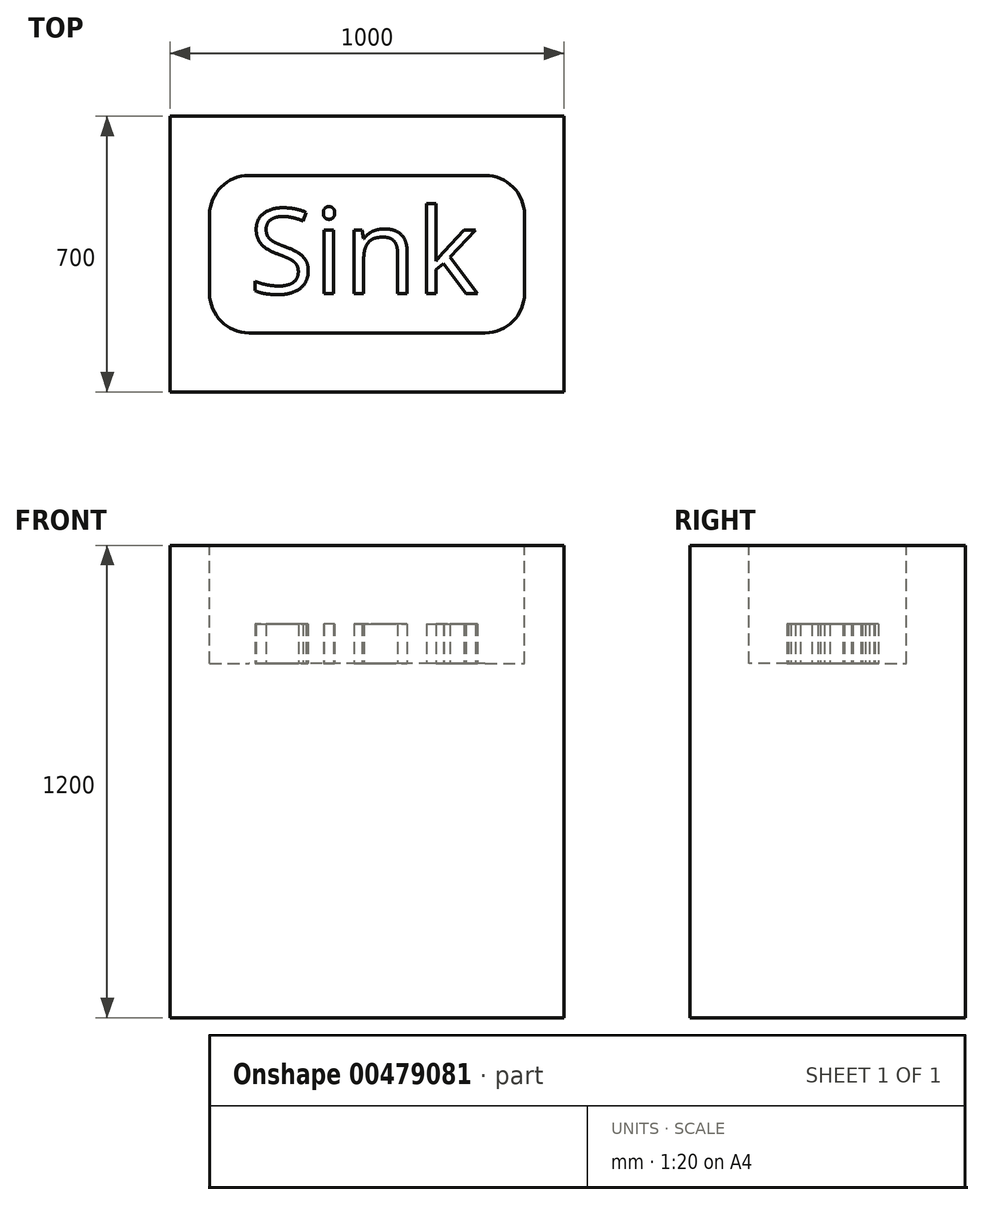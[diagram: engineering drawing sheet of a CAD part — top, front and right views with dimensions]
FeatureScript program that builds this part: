
annotation { "Feature Type Name" : "Feature", "Feature Type Description" : "" }
export const myFeature = defineFeature(function(context is Context, id is Id, definition is map)
    precondition{}
    {
        {
            var Q0;
            Q0=qCreatedBy(makeId("Top.planeOp"),FACE);
            var sketch = newSketch(context, id + "F0", { "sketchPlane" : qUnion([Q0])});
            skLineSegment(sketch, "E0.bottom", {"start": v(500, -350) * mm, "end": v(-500, -350) * mm});
            skLineSegment(sketch, "E0.top", {"start": v(500, 350) * mm, "end": v(-500, 350) * mm});
            skLineSegment(sketch, "E0.left", {"start": v(500, -350) * mm, "end": v(500, 350) * mm});
            skLineSegment(sketch, "E0.right", {"start": v(-500, -350) * mm, "end": v(-500, 350) * mm});
            skPoint(sketch, "E0.middle", {"position": v(0, 0) * mm});
            skSolve(sketch);
        }
        {
            var Q0;
            Q0 = qSketchRegion(id + "F0", true);
            extrude(context, id + "F1", {"entities" : qUnion([Q0]), "depth" : 1200 * mm});
        }
        {
            var Q0;
            Q0=makeQuery(id+"F1.opExtrude","CAP_FACE",FACE,{"disambiguationData":[OSD([sQuery(id+"F0.wireOp",EDGE,"E0.bottom"),sQuery(id+"F0.wireOp",EDGE,"E0.top"),sQuery(id+"F0.wireOp",EDGE,"E0.left"),sQuery(id+"F0.wireOp",EDGE,"E0.right")])],"isStart":false});
            var sketch = newSketch(context, id + "F2", { "sketchPlane" : qUnion([Q0])});
            skLineSegment(sketch, "E1.bottom", {"start": v(300, -200) * mm, "end": v(-300, -200) * mm});
            skLineSegment(sketch, "E1.top", {"start": v(300, 200) * mm, "end": v(-300, 200) * mm});
            skLineSegment(sketch, "E1.left", {"start": v(400, -100) * mm, "end": v(400, 100) * mm});
            skLineSegment(sketch, "E1.right", {"start": v(-400, -100) * mm, "end": v(-400, 100) * mm});
            skPoint(sketch, "E1.middle", {"position": v(0, 0) * mm});
            skPoint(sketch, "E2.visualSharp", {"position": v(-400, 200) * mm});
            skArc(sketch, "E2.filletArc", {"start": v(-300, 200) * mm, "mid": v(-370.71, 170.71) * mm, "end": v(-400, 100) * mm});
            skPoint(sketch, "E3.visualSharp", {"position": v(-400, -200) * mm});
            skArc(sketch, "E3.filletArc", {"start": v(-400, -100) * mm, "mid": v(-370.71, -170.71) * mm, "end": v(-300, -200) * mm});
            skPoint(sketch, "E4.visualSharp", {"position": v(400, -200) * mm});
            skArc(sketch, "E4.filletArc", {"start": v(300, -200) * mm, "mid": v(370.71, -170.71) * mm, "end": v(400, -100) * mm});
            skPoint(sketch, "E5.visualSharp", {"position": v(400, 200) * mm});
            skArc(sketch, "E5.filletArc", {"start": v(400, 100) * mm, "mid": v(370.71, 170.71) * mm, "end": v(300, 200) * mm});
            skSolve(sketch);
        }
        {
            var Q0;
            Q0 = qSketchRegion(id + "F2", true);
            extrude(context, id + "F3", {"entities" : qUnion([Q0]), "operationType" : NewBodyOperationType.REMOVE, "oppositeDirection" : true, "depth" : 300 * mm});
        }
        {
            var Q0;
            Q0=makeQuery(id+"F3.boolean.opBoolean","COPY",FACE,{"derivedFrom":makeQuery(id+"F3.opExtrude","CAP_FACE",FACE,{"disambiguationData":[OSD([sQuery(id+"F2.wireOp",EDGE,"E1.bottom"),sQuery(id+"F2.wireOp",EDGE,"E1.top"),sQuery(id+"F2.wireOp",EDGE,"E1.left"),sQuery(id+"F2.wireOp",EDGE,"E1.right"),sQuery(id+"F2.wireOp",EDGE,"E2.filletArc"),sQuery(id+"F2.wireOp",EDGE,"E3.filletArc"),sQuery(id+"F2.wireOp",EDGE,"E4.filletArc"),sQuery(id+"F2.wireOp",EDGE,"E5.filletArc")])],"isStart":false})});
            var sketch = newSketch(context, id + "F4", { "sketchPlane" : qUnion([Q0])});
            skText(sketch, "E6", { "text": "Sink", "fontName": "OpenSans-Regular.ttf"});
            const initialGuessF4  = {"E6": [-0.3, -0.1, 1, 0, 0.21658]};
            skSetInitialGuess(sketch, initialGuessF4);
            skSolve(sketch);
        }
        {
            var Q0;
            Q0 = qSketchRegion(id + "F4", true);
            extrude(context, id + "F5", {"entities" : qUnion([Q0]), "operationType" : NewBodyOperationType.ADD, "depth" : 100 * mm});
        }
    });
